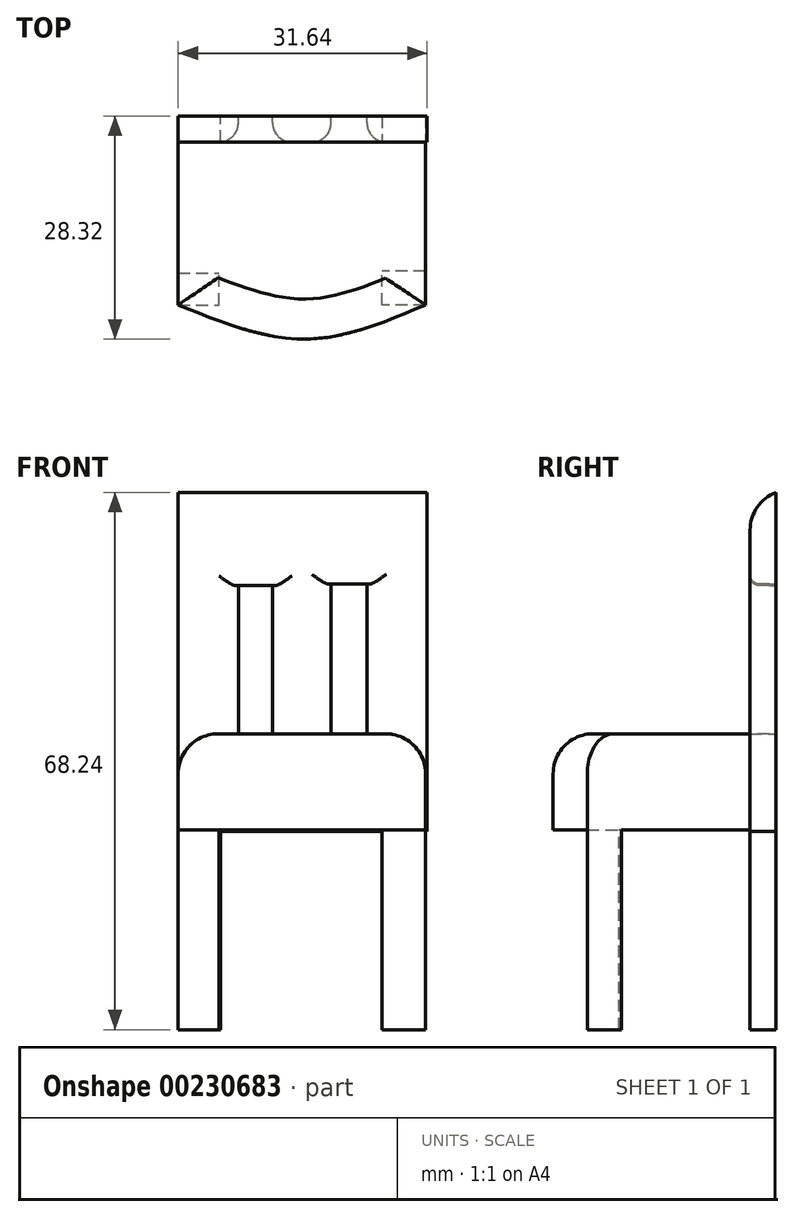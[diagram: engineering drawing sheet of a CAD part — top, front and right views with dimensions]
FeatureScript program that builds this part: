
annotation { "Feature Type Name" : "Feature", "Feature Type Description" : "" }
export const myFeature = defineFeature(function(context is Context, id is Id, definition is map)
    precondition{}
    {
        {
            var Q0;
            Q0=qCreatedBy(makeId("Front.planeOp"),FACE);
            var sketch = newSketch(context, id + "F0", { "sketchPlane" : qUnion([Q0])});
            skLineSegment(sketch, "E0.bottom", {"start": v(-16.13, 30.4) * mm, "end": v(15.5, 30.4) * mm});
            skLineSegment(sketch, "E0.top", {"start": v(-16.13, -12.4) * mm, "end": v(15.5, -12.4) * mm});
            skLineSegment(sketch, "E0.left", {"start": v(-16.13, 30.4) * mm, "end": v(-16.13, -12.4) * mm});
            skLineSegment(sketch, "E0.right", {"start": v(15.5, 30.4) * mm, "end": v(15.5, -12.4) * mm});
            skLineSegment(sketch, "E1.bottom", {"start": v(-8.48, 18.81) * mm, "end": v(-4.13, 18.81) * mm});
            skLineSegment(sketch, "E1.top", {"start": v(-8.48, 0) * mm, "end": v(-4.13, 0) * mm});
            skLineSegment(sketch, "E1.left", {"start": v(-8.48, 18.81) * mm, "end": v(-8.48, 0) * mm});
            skLineSegment(sketch, "E1.right", {"start": v(-4.13, 18.81) * mm, "end": v(-4.13, 0) * mm});
            skLineSegment(sketch, "E2.bottom", {"start": v(3.3, 19.02) * mm, "end": v(7.86, 19.02) * mm});
            skLineSegment(sketch, "E2.top", {"start": v(3.3, 0) * mm, "end": v(7.86, 0) * mm});
            skLineSegment(sketch, "E2.left", {"start": v(3.3, 19.02) * mm, "end": v(3.3, 0) * mm});
            skLineSegment(sketch, "E2.right", {"start": v(7.86, 19.02) * mm, "end": v(7.86, 0) * mm});
            skSolve(sketch);
        }
        {
            var Q0;
            Q0=makeQuery(id+"F0.imprint","IMPRINT",FACE,{"disambiguationData":[TD([[makeQuery(id+"F0.imprint","IMPRINT",EDGE,{"derivedFrom":sQuery(id+"F0.wireOp",EDGE,"E0.bottom")}),-1.0]])]});
            extrude(context, id + "F1", {"entities" : qUnion([Q0]), "depth" : 3.3 * mm});
        }
        {
            var Q0;
            Q0=qCreatedBy(makeId("Top.planeOp"),FACE);
            var sketch = newSketch(context, id + "F2", { "sketchPlane" : qUnion([Q0])});
            skLineSegment(sketch, "E3", {"start": v(-16.13, -5.38) * mm, "end": v(-16.13, -23.98) * mm});
            skLineSegment(sketch, "E4", {"start": v(15.3, -5.17) * mm, "end": v(15.3, -23.98) * mm});
            skFitSpline(sketch, "E5", {"points": [v(-16.13, -23.98) * mm, v(0, -28.32) * mm, v(15.3, -23.98) * mm], "startDerivative": vector(32.09, -12.97) * mm, "endDerivative": vector(30.76, 13.08) * mm});
            skLineSegment(sketch, "E6", {"start": v(-16.13, -5.38) * mm, "end": v(-16.13, -3.06) * mm});
            skLineSegment(sketch, "E7", {"start": v(-16.13, -3.06) * mm, "end": v(15.3, -3.06) * mm});
            skPoint(sketch, "E7.endSnap0", {"position": v(15.3, -14.58) * mm});
            skLineSegment(sketch, "E8", {"start": v(15.3, -3.06) * mm, "end": v(15.3, -5.17) * mm});
            skSolve(sketch);
        }
        {
            var Q0;
            Q0=makeQuery(id+"F1.opExtrude","SWEPT_FACE",FACE,{"disambiguationData":[OSD([sQuery(id+"F0.wireOp",EDGE,"E0.bottom")])]});
            extrude(context, id + "F3", {"entities" : qUnion([Q0]), "operationType" : NewBodyOperationType.ADD, "depth" : 0.25 * mm});
        }
        {
            var Q0;
            Q0=makeQuery(id+"F2.imprint","IMPRINT",FACE,{"disambiguationData":[TD([[makeQuery(id+"F2.imprint","IMPRINT",EDGE,{"derivedFrom":sQuery(id+"F2.wireOp",EDGE,"E3")}),1.0]])]});
            extrude(context, id + "F4", {"entities" : qUnion([Q0]), "operationType" : NewBodyOperationType.ADD, "oppositeDirection" : true, "depth" : 12.2 * mm});
        }
        {
            var Q0;
            Q0=makeQuery(id+"F4.boolean.opBoolean","MERGE",FACE,{"derivedFrom":[makeQuery(id+"F1.opExtrude","SWEPT_FACE",FACE,{"disambiguationData":[OSD([sQuery(id+"F0.wireOp",EDGE,"E1.top")])]}),makeQuery(id+"F1.opExtrude","SWEPT_FACE",FACE,{"disambiguationData":[OSD([sQuery(id+"F0.wireOp",EDGE,"E2.top")])]}),makeQuery(id+"F4.opExtrude","CAP_FACE",FACE,{"disambiguationData":[OSD([sQuery(id+"F2.wireOp",EDGE,"E3"),sQuery(id+"F2.wireOp",EDGE,"E4"),sQuery(id+"F2.wireOp",EDGE,"E5"),sQuery(id+"F2.wireOp",EDGE,"E6"),sQuery(id+"F2.wireOp",EDGE,"E7"),sQuery(id+"F2.wireOp",EDGE,"E8")])],"isStart":true})]});
            extrude(context, id + "F5", {"entities" : qUnion([Q0]), "operationType" : NewBodyOperationType.ADD, "oppositeDirection" : true, "depth" : 7.62 * mm});
        }
        {
            var Q0;
            Q0=makeQuery(id+"F4.boolean.opBoolean","MERGE",FACE,{"derivedFrom":[makeQuery(id+"F1.opExtrude","SWEPT_FACE",FACE,{"disambiguationData":[OSD([sQuery(id+"F0.wireOp",EDGE,"E1.top")])]}),makeQuery(id+"F1.opExtrude","SWEPT_FACE",FACE,{"disambiguationData":[OSD([sQuery(id+"F0.wireOp",EDGE,"E2.top")])]}),makeQuery(id+"F4.opExtrude","CAP_FACE",FACE,{"disambiguationData":[OSD([sQuery(id+"F2.wireOp",EDGE,"E3"),sQuery(id+"F2.wireOp",EDGE,"E4"),sQuery(id+"F2.wireOp",EDGE,"E5"),sQuery(id+"F2.wireOp",EDGE,"E6"),sQuery(id+"F2.wireOp",EDGE,"E7"),sQuery(id+"F2.wireOp",EDGE,"E8")])],"isStart":true})]});
            extrude(context, id + "F6", {"entities" : qUnion([Q0]), "operationType" : NewBodyOperationType.ADD, "oppositeDirection" : true, "depth" : 7.37 * mm});
        }
        {
            var Q0;
            Q0=makeQuery(id+"F4.opExtrude","CAP_EDGE",EDGE,{"disambiguationData":[OSD([sQuery(id+"F2.wireOp",EDGE,"E5")])],"isStart":true});
            var Q1;
            Q1=makeQuery(id+"F4.opExtrude","CAP_EDGE",EDGE,{"disambiguationData":[OSD([sQuery(id+"F2.wireOp",EDGE,"E4"),sQuery(id+"F2.wireOp",EDGE,"E8")])],"isStart":true});
            var Q2;
            Q2=makeQuery(id+"F4.opExtrude","CAP_EDGE",EDGE,{"disambiguationData":[OSD([sQuery(id+"F2.wireOp",EDGE,"E3"),sQuery(id+"F2.wireOp",EDGE,"E6")])],"isStart":true});
            fillet(context, id + "F7", {"entities" : qUnion([Q0, Q1, Q2]), "radius" : 5.08 * mm, "tangentPropagation" : true, "allowEdgeOverflow" : false});
        }
        {
            var Q0;
            {var subQ0=sQuery(id+"F0.wireOp",EDGE,"E0.bottom");Q0=makeQuery(id+"F3.opExtrude","CAP_EDGE",EDGE,{"disambiguationData":[OSD([subQ0]),TDD([makeQuery(id+"F1.opExtrude","CAP_EDGE",EDGE,{"disambiguationData":[OSD([subQ0])],"isStart":false})])],"isStart":false});}
            fillet(context, id + "F8", {"entities" : qUnion([Q0]), "radius" : 5.08 * mm, "tangentPropagation" : true, "allowEdgeOverflow" : false});
        }
        {
            var Q0;
            Q0=makeQuery(id+"F4.opExtrude","CAP_FACE",FACE,{"disambiguationData":[OSD([sQuery(id+"F2.wireOp",EDGE,"E3"),sQuery(id+"F2.wireOp",EDGE,"E4"),sQuery(id+"F2.wireOp",EDGE,"E5"),sQuery(id+"F2.wireOp",EDGE,"E6"),sQuery(id+"F2.wireOp",EDGE,"E7"),sQuery(id+"F2.wireOp",EDGE,"E8")])],"isStart":false});
            var sketch = newSketch(context, id + "F9", { "sketchPlane" : qUnion([Q0])});
            skLineSegment(sketch, "E9.bottom", {"start": v(-16.13, 23.98) * mm, "end": v(-10.96, 23.98) * mm});
            skLineSegment(sketch, "E9.top", {"start": v(-16.13, 19.95) * mm, "end": v(-10.96, 19.95) * mm});
            skLineSegment(sketch, "E9.left", {"start": v(-16.13, 23.98) * mm, "end": v(-16.13, 19.95) * mm});
            skLineSegment(sketch, "E9.right", {"start": v(-10.96, 23.98) * mm, "end": v(-10.96, 19.95) * mm});
            skLineSegment(sketch, "E10.bottom", {"start": v(15.3, 23.98) * mm, "end": v(9.75, 23.98) * mm});
            skLineSegment(sketch, "E10.top", {"start": v(15.3, 19.67) * mm, "end": v(9.75, 19.67) * mm});
            skLineSegment(sketch, "E10.left", {"start": v(15.3, 23.98) * mm, "end": v(15.3, 19.67) * mm});
            skLineSegment(sketch, "E10.right", {"start": v(9.75, 23.98) * mm, "end": v(9.75, 19.67) * mm});
            skLineSegment(sketch, "E11.bottom", {"start": v(15.3, 0) * mm, "end": v(9.75, 0) * mm});
            skLineSegment(sketch, "E11.top", {"start": v(15.3, 3.3) * mm, "end": v(9.75, 3.3) * mm});
            skLineSegment(sketch, "E11.left", {"start": v(15.3, 0) * mm, "end": v(15.3, 3.3) * mm});
            skLineSegment(sketch, "E11.right", {"start": v(9.75, 0) * mm, "end": v(9.75, 3.3) * mm});
            skPoint(sketch, "E12.oppositeSnap0", {"position": v(12.52, 0) * mm});
            skLineSegment(sketch, "E12.bottom", {"start": v(-16.13, 3.3) * mm, "end": v(-10.75, 3.3) * mm});
            skLineSegment(sketch, "E12.top", {"start": v(-16.13, 0) * mm, "end": v(-10.75, 0) * mm});
            skLineSegment(sketch, "E12.left", {"start": v(-16.13, 3.3) * mm, "end": v(-16.13, 0) * mm});
            skLineSegment(sketch, "E12.right", {"start": v(-10.75, 3.3) * mm, "end": v(-10.75, 0) * mm});
            skSolve(sketch);
        }
        {
            var Q0;
            Q0 = qSketchRegion(id + "F9", true);
            extrude(context, id + "F10", {"entities" : qUnion([Q0]), "operationType" : NewBodyOperationType.ADD, "depth" : 25.4 * mm});
        }
        {
            var Q0;
            Q0=makeQuery(id+"F1.opExtrude","CAP_EDGE",EDGE,{"disambiguationData":[OSD([sQuery(id+"F0.wireOp",EDGE,"E1.left")])],"isStart":false});
            var Q1;
            Q1=makeQuery(id+"F1.opExtrude","CAP_EDGE",EDGE,{"disambiguationData":[OSD([sQuery(id+"F0.wireOp",EDGE,"E2.right")])],"isStart":false});
            var Q2;
            Q2=makeQuery(id+"F1.opExtrude","CAP_EDGE",EDGE,{"disambiguationData":[OSD([sQuery(id+"F0.wireOp",EDGE,"E2.left")])],"isStart":false});
            var Q3;
            Q3=makeQuery(id+"F1.opExtrude","CAP_EDGE",EDGE,{"disambiguationData":[OSD([sQuery(id+"F0.wireOp",EDGE,"E1.right")])],"isStart":false});
            fillet(context, id + "F11", {"entities" : qUnion([Q0, Q1, Q2, Q3]), "radius" : 2.45 * mm, "tangentPropagation" : true, "allowEdgeOverflow" : false});
        }
        {
            var Q0;
            Q0=makeQuery(id+"F1.opExtrude","CAP_EDGE",EDGE,{"disambiguationData":[OSD([sQuery(id+"F0.wireOp",EDGE,"E2.bottom")])],"isStart":false});
            var Q1;
            Q1=makeQuery(id+"F1.opExtrude","CAP_EDGE",EDGE,{"disambiguationData":[OSD([sQuery(id+"F0.wireOp",EDGE,"E1.bottom")])],"isStart":false});
            fillet(context, id + "F12", {"entities" : qUnion([Q0, Q1]), "radius" : 1.23 * mm, "tangentPropagation" : true, "allowEdgeOverflow" : false});
        }
    });
